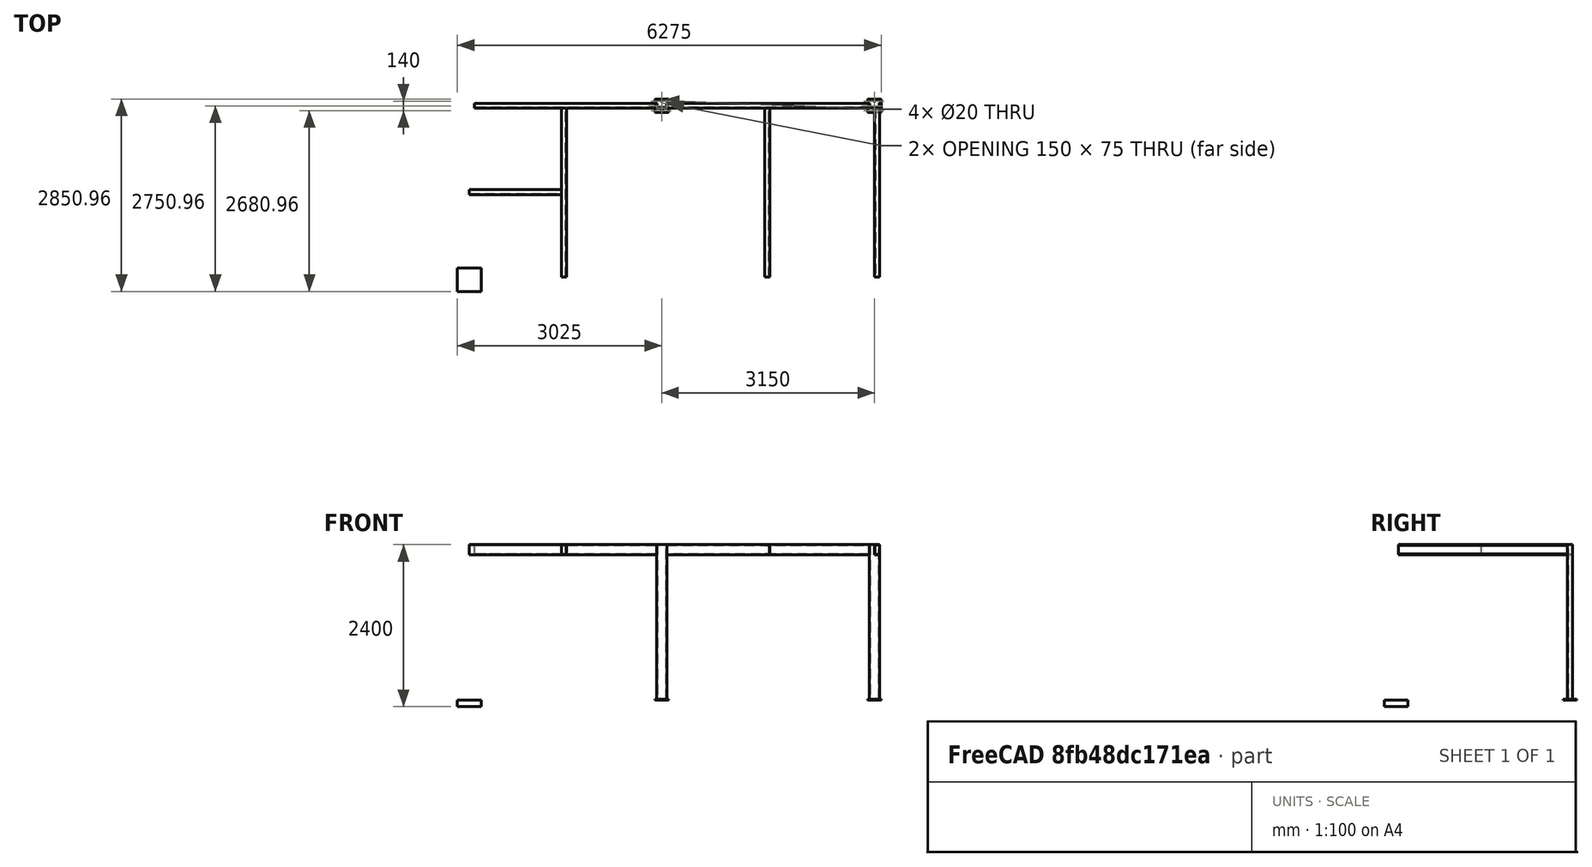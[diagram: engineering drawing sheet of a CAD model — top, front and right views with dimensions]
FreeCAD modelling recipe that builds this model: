
FCSTD DOCUMENT  (FreeCAD 0.21R30492 (Git))
Label: test
License: All rights reserved
LicenseURL: http://en.wikipedia.org/wiki/All_rights_reserved
objects: App::FeaturePython×44, Part::FeaturePython×14, Part::Mirroring×3, Part::Extrusion×2, App::Link×2, Part::MultiFuse×1
note: 20 computed .brp shape members not serialized (recipe doc carries the construction recipe); baked Part::Feature solids carry a one-line shape summary decoded from their .brp

FEATURE [Part::FeaturePython] Rectang  # WARN: FeaturePython — macro-defined, semantics opaque (R4)
  B = 350
  H = 350
  sface = 0
FEATURE [Part::Extrusion] Extrude
  Base = -> Rectang
  Dir = (0,0,-1)
  DirMode = 2
  FaceMakerClass = Part::FaceMakerBullseye
  LengthFwd = 100
  LengthRev = 0
  Solid = false
  Symmetric = false
FEATURE [Part::FeaturePython] Extrude_001  # a2plus imported part (geometry in sourceFile) (typed FeaturePython)
  a2p_Version = 0.4.60i
  fixedPosition = true
  localSourceObject = Extrude
  objectType = a2pPart
  sourceFile = converted
  subassemblyImport = false
  timeLastImport = 1.67808e+09
  updateColors = true
FEATURE [Part::FeaturePython] BasePlate  # WARN: FeaturePython — macro-defined, semantics opaque (R4)
  B = 200
  D = 20
  H = 200
  b1 = 30
  h1 = 100
  sface = 0
FEATURE [Part::FeaturePython] C150x75x6  label="SS"  # WARN: FeaturePython — macro-defined, semantics opaque (R4)
  L = 2300
  Solid = true
  size = 3
  standard = SS
  expr: Label = standard
FEATURE [Part::Extrusion] Extrude001
  Base = -> BasePlate
  Dir = (0,0,1)
  DirMode = 2
  FaceMakerClass = Part::FaceMakerBullseye
  LengthFwd = 9
  LengthRev = 0
  Solid = true
  Symmetric = false
FEATURE [Part::MultiFuse] Fusion  label="C-shaped steel"
  Placement = pos=(-7.12519e-09,0.956326,3.2e-14) rot=(0,0,-1;1.5708rad)
  Shapes = -> [C150x75x6,Extrude001]
FEATURE [App::FeaturePython] centerOfMass_001  label="centerOfMass_001__Extrude_001"  # a2plus constraint (typed FeaturePython)
  Object1 = Fusion
  Object2 = Extrude_001
  ParentTreeObject = -> Fusion
  SubElement1 = Face2
  SubElement2 = Face5
  Suppressed = false
  Type = CenterOfMass
  directionConstraint = 1
  lockRotation = false
  offset = 0
FEATURE [App::FeaturePython] centerOfMass_001_mirror  label="centerOfMass_001__C-shaped steel"  # a2plus constraint (typed FeaturePython)
  Object1 = Fusion
  Object2 = Extrude_001
  ParentTreeObject = -> Extrude_001
  SubElement1 = Face2
  SubElement2 = Face5
  Suppressed = false
  Type = CenterOfMass
  directionConstraint = 1
  lockRotation = false
  offset = 0
FEATURE [Part::FeaturePython] C150x75x007  label="Channel"  # WARN: FeaturePython — macro-defined, semantics opaque (R4)
  L = 2700
  Placement = pos=(2775,0.956326,2225) rot=(0.57735,-0.57735,-0.57735;2.0944rad)
  Solid = true
  size = 3
  standard = SS
FEATURE [App::FeaturePython] pointIdentity_001  label="pointIdentity_001__C-shaped steel"  # a2plus constraint (typed FeaturePython)
  Object1 = C150x75x007
  Object2 = Fusion
  ParentTreeObject = -> C150x75x007
  SubElement1 = Vertex2
  SubElement2 = Vertex38
  Suppressed = false
  Type = pointIdentity
FEATURE [App::FeaturePython] pointIdentity_001_mirror  label="pointIdentity_001__Channel"  # a2plus constraint (typed FeaturePython)
  Object1 = C150x75x007
  Object2 = Fusion
  ParentTreeObject = -> Fusion
  SubElement1 = Vertex2
  SubElement2 = Vertex38
  Suppressed = false
  Type = pointIdentity
FEATURE [App::Link] Link  label="C-shaped steel001"
  LinkPlacement = pos=(2850,0.956314,-1.98657e-07) rot=(0,0,-1;1.5708rad)
  LinkedObject = -> Fusion
  Placement = pos=(2850,0.956314,-1.98657e-07) rot=(0,0,-1;1.5708rad)
FEATURE [App::FeaturePython] pointIdentity_002  label="pointIdentity_002__C-shaped steel001"  # a2plus constraint (typed FeaturePython)
  Object1 = C150x75x007
  Object2 = Link
  ParentTreeObject = -> C150x75x007
  SubElement1 = Vertex1
  SubElement2 = Vertex37
  Suppressed = false
  Type = pointIdentity
FEATURE [App::FeaturePython] pointIdentity_002_mirror  label="pointIdentity_002__Channel"  # a2plus constraint (typed FeaturePython)
  Object1 = C150x75x007
  Object2 = Link
  ParentTreeObject = -> Link
  SubElement1 = Vertex1
  SubElement2 = Vertex37
  Suppressed = false
  Type = pointIdentity
FEATURE [Part::FeaturePython] C150x75x008  label="Channel001"  # WARN: FeaturePython — macro-defined, semantics opaque (R4)
  L = 3000
  Placement = pos=(5925,0.956301,2225) rot=(0.57735,-0.57735,-0.57735;2.0944rad)
  Solid = true
  size = 3
  standard = SS
FEATURE [App::FeaturePython] pointIdentity_003  label="pointIdentity_003__C-shaped steel001"  # a2plus constraint (typed FeaturePython)
  Object1 = C150x75x008
  Object2 = Link
  ParentTreeObject = -> C150x75x008
  SubElement1 = Vertex2
  SubElement2 = Vertex38
  Suppressed = false
  Type = pointIdentity
FEATURE [App::FeaturePython] pointIdentity_003_mirror  label="pointIdentity_003__Channel001"  # a2plus constraint (typed FeaturePython)
  Object1 = C150x75x008
  Object2 = Link
  ParentTreeObject = -> Link
  SubElement1 = Vertex2
  SubElement2 = Vertex38
  Suppressed = false
  Type = pointIdentity
FEATURE [App::Link] Link001  label="C-shaped steel002"
  LinkPlacement = pos=(6000,0.956288,-2.23239e-07) rot=(0,0,-1;1.5708rad)
  LinkedObject = -> Link
  Placement = pos=(6000,0.956288,-2.23239e-07) rot=(0,0,-1;1.5708rad)
FEATURE [App::FeaturePython] pointIdentity_004  label="pointIdentity_004__Channel001"  # a2plus constraint (typed FeaturePython)
  Object1 = Link001
  Object2 = C150x75x008
  ParentTreeObject = -> Link001
  SubElement1 = Vertex37
  SubElement2 = Vertex1
  Suppressed = false
  Type = pointIdentity
FEATURE [App::FeaturePython] pointIdentity_004_mirror  label="pointIdentity_004__C-shaped steel002"  # a2plus constraint (typed FeaturePython)
  Object1 = Link001
  Object2 = C150x75x008
  ParentTreeObject = -> C150x75x008
  SubElement1 = Vertex37
  SubElement2 = Vertex1
  Suppressed = false
  Type = pointIdentity
FEATURE [Part::FeaturePython] C150x75x009  label="Channel002"  # WARN: FeaturePython — macro-defined, semantics opaque (R4)
  L = 2500
  Placement = pos=(-37.5,38.4563,2225) rot=(0,0.707107,0.707107;3.14159rad)
  Solid = true
  size = 3
  standard = SS
FEATURE [App::FeaturePython] pointIdentity_005  label="pointIdentity_005__C-shaped steel"  # a2plus constraint (typed FeaturePython)
  Object1 = C150x75x009
  Object2 = Fusion
  ParentTreeObject = -> C150x75x009
  SubElement1 = Vertex23
  SubElement2 = Vertex37
  Suppressed = false
  Type = pointIdentity
FEATURE [App::FeaturePython] pointIdentity_005_mirror  label="pointIdentity_005__Channel002"  # a2plus constraint (typed FeaturePython)
  Object1 = C150x75x009
  Object2 = Fusion
  ParentTreeObject = -> Fusion
  SubElement1 = Vertex23
  SubElement2 = Vertex37
  Suppressed = false
  Type = pointIdentity
FEATURE [Part::FeaturePython] Clone  label="Channel003"  # Draft clone (typed FeaturePython)
  AttacherType = Attacher::AttachEngine3D
  Fuse = false
  Objects = -> [C150x75x009]
  Placement = pos=(2850,38.4563,2225) rot=(0,0.707107,0.707107;3.14159rad)
  Scale = (1,1,1)
FEATURE [App::FeaturePython] pointOnLine_001  label="pointOnLine_001__C-shaped steel001"  # a2plus constraint (typed FeaturePython)
  Object1 = Clone
  Object2 = Link
  ParentTreeObject = -> Clone
  SubElement1 = Vertex1
  SubElement2 = Edge44
  Suppressed = false
  Type = pointOnLine
FEATURE [App::FeaturePython] pointOnLine_001_mirror  label="pointOnLine_001__Channel003"  # a2plus constraint (typed FeaturePython)
  Object1 = Clone
  Object2 = Link
  ParentTreeObject = -> Link
  SubElement1 = Vertex1
  SubElement2 = Edge44
  Suppressed = false
  Type = pointOnLine
FEATURE [App::FeaturePython] planeCoincident_001  label="planeCoincident_001__C-shaped steel001"  # a2plus constraint (typed FeaturePython)
  Object1 = Clone
  Object2 = Link
  ParentTreeObject = -> Clone
  SubElement1 = Face1
  SubElement2 = Face21
  Suppressed = false
  Type = plane
  directionConstraint = 0
  offset = 37.5
FEATURE [App::FeaturePython] planeCoincident_001_mirror  label="planeCoincident_001__Channel003"  # a2plus constraint (typed FeaturePython)
  Object1 = Clone
  Object2 = Link
  ParentTreeObject = -> Link
  SubElement1 = Face1
  SubElement2 = Face21
  Suppressed = false
  Type = plane
  directionConstraint = 0
  offset = 37.5
FEATURE [Part::FeaturePython] Clone001  label="Channel004"  # Draft clone (typed FeaturePython)
  AttacherType = Attacher::AttachEngine3D
  Fuse = false
  Objects = -> [Clone]
  Placement = pos=(6037.5,2538.46,2225) rot=(1,0,0;1.5708rad)
  Scale = (1,1,1)
FEATURE [App::FeaturePython] pointIdentity_006  label="pointIdentity_006__Channel004"  # a2plus constraint (typed FeaturePython)
  Object1 = Link001
  Object2 = Clone001
  ParentTreeObject = -> Link001
  SubElement1 = Vertex38
  SubElement2 = Vertex24
  Suppressed = false
  Type = pointIdentity
FEATURE [App::FeaturePython] pointIdentity_006_mirror  label="pointIdentity_006__C-shaped steel002"  # a2plus constraint (typed FeaturePython)
  Object1 = Link001
  Object2 = Clone001
  ParentTreeObject = -> Clone001
  SubElement1 = Vertex38
  SubElement2 = Vertex24
  Suppressed = false
  Type = pointIdentity
FEATURE [Part::FeaturePython] Clone002  label="C-shaped steel003"  # Draft clone (typed FeaturePython)
  AttacherType = Attacher::AttachEngine3D
  Fuse = false
  Objects = -> [Fusion]
  Placement = pos=(0.00420855,2575.96,5.04641e-05) rot=(-1e-06,-1e-06,1;1.5708rad)
  Scale = (1,1,1)
FEATURE [App::FeaturePython] pointIdentity_007  label="pointIdentity_007__Channel002"  # a2plus constraint (typed FeaturePython)
  Object1 = Clone002
  Object2 = C150x75x009
  ParentTreeObject = -> Clone002
  SubElement1 = Vertex38
  SubElement2 = Vertex24
  Suppressed = false
  Type = pointIdentity
FEATURE [App::FeaturePython] pointIdentity_007_mirror  label="pointIdentity_007__C-shaped steel003"  # a2plus constraint (typed FeaturePython)
  Object1 = Clone002
  Object2 = C150x75x009
  ParentTreeObject = -> C150x75x009
  SubElement1 = Vertex38
  SubElement2 = Vertex24
  Suppressed = false
  Type = pointIdentity
FEATURE [Part::FeaturePython] Clone003  label="C-shaped steel004"  # Draft clone (typed FeaturePython)
  AttacherType = Attacher::AttachEngine3D
  Fuse = false
  Objects = -> [Clone002]
  Placement = pos=(2850,2575.96,0.000160857) rot=(0,0,1;1.5708rad)
  Scale = (1,1,1)
FEATURE [App::FeaturePython] planeCoincident_002  label="planeCoincident_002__Channel003"  # a2plus constraint (typed FeaturePython)
  Object1 = Clone003
  Object2 = Clone
  ParentTreeObject = -> Clone003
  SubElement1 = Face11
  SubElement2 = Face1
  Suppressed = false
  Type = plane
  directionConstraint = 0
  offset = -37.5
FEATURE [App::FeaturePython] planeCoincident_002_mirror  label="planeCoincident_002__C-shaped steel004"  # a2plus constraint (typed FeaturePython)
  Object1 = Clone003
  Object2 = Clone
  ParentTreeObject = -> Clone
  SubElement1 = Face11
  SubElement2 = Face1
  Suppressed = false
  Type = plane
  directionConstraint = 0
  offset = -37.5
FEATURE [Part::Mirroring] mirror  label="Channel (mirrored) "
  Base = (-7.12504e-09,1288.46,2300)
  Normal = (-2.6766e-09,-1,0)
  Placement = pos=(-6.69189e-06,4.01514e-07,0.000100336) rot=(0,0,1;0rad)
  Source = -> C150x75x007
FEATURE [App::FeaturePython] pointIdentity_008  label="pointIdentity_008__C-shaped steel003"  # a2plus constraint (typed FeaturePython)
  Object1 = mirror
  Object2 = Clone002
  ParentTreeObject = -> mirror
  SubElement1 = Vertex2
  SubElement2 = Vertex37
  Suppressed = false
  Type = pointIdentity
FEATURE [App::FeaturePython] pointIdentity_008_mirror  label="pointIdentity_008__Channel (mirrored) "  # a2plus constraint (typed FeaturePython)
  Object1 = mirror
  Object2 = Clone002
  ParentTreeObject = -> Clone002
  SubElement1 = Vertex2
  SubElement2 = Vertex37
  Suppressed = false
  Type = pointIdentity
FEATURE [Part::Mirroring] mirror001  label="Channel001 (mirrored) "
  Base = (2870.13,1288.46,2189.53)
  Normal = (-9.07043e-09,-1,0)
  Placement = pos=(0.000400686,2.25227e-05,0.000250762) rot=(0,0,1;0rad)
  Source = -> C150x75x008
FEATURE [App::FeaturePython] pointIdentity_009  label="pointIdentity_009__C-shaped steel004"  # a2plus constraint (typed FeaturePython)
  Object1 = mirror001
  Object2 = Clone003
  ParentTreeObject = -> mirror001
  SubElement1 = Vertex2
  SubElement2 = Vertex37
  Suppressed = false
  Type = pointIdentity
FEATURE [App::FeaturePython] pointIdentity_009_mirror  label="pointIdentity_009__Channel001 (mirrored) "  # a2plus constraint (typed FeaturePython)
  Object1 = mirror001
  Object2 = Clone003
  ParentTreeObject = -> Clone003
  SubElement1 = Vertex2
  SubElement2 = Vertex37
  Suppressed = false
  Type = pointIdentity
FEATURE [Part::Mirroring] mirror002  label="C-shaped steel002 (mirrored) "
  Base = (2870.13,1288.46,2189.53)
  Normal = (-6.98352e-09,-1,0)
  Placement = pos=(0.000363814,-2.37563e-05,3.179e-06) rot=(0,0,1;0rad)
  Source = -> Link001
FEATURE [App::FeaturePython] pointIdentity_010  label="pointIdentity_010__Channel004"  # a2plus constraint (typed FeaturePython)
  Object1 = mirror002
  Object2 = Clone001
  ParentTreeObject = -> mirror002
  SubElement1 = Vertex38
  SubElement2 = Vertex23
  Suppressed = false
  Type = pointIdentity
FEATURE [App::FeaturePython] pointIdentity_010_mirror  label="pointIdentity_010__C-shaped steel002 (mirrored) "  # a2plus constraint (typed FeaturePython)
  Object1 = mirror002
  Object2 = Clone001
  ParentTreeObject = -> Clone001
  SubElement1 = Vertex38
  SubElement2 = Vertex23
  Suppressed = false
  Type = pointIdentity
FEATURE [Part::FeaturePython] Clone004  label="Channel005"  # Draft clone (typed FeaturePython)
  AttacherType = Attacher::AttachEngine3D
  Fuse = false
  Objects = -> [C150x75x009]
  Placement = pos=(1405,38.4563,2225) rot=(0,0.707107,0.707107;3.14159rad)
  Scale = (1,1,1)
FEATURE [App::FeaturePython] planeCoincident_003  label="planeCoincident_003__Channel005"  # a2plus constraint (typed FeaturePython)
  Object1 = Clone
  Object2 = Clone004
  ParentTreeObject = -> Clone
  SubElement1 = Face1
  SubElement2 = Face1
  Suppressed = false
  Type = plane
  directionConstraint = 0
  offset = -1445
FEATURE [App::FeaturePython] planeCoincident_003_mirror  label="planeCoincident_003__Channel003"  # a2plus constraint (typed FeaturePython)
  Object1 = Clone
  Object2 = Clone004
  ParentTreeObject = -> Clone004
  SubElement1 = Face1
  SubElement2 = Face1
  Suppressed = false
  Type = plane
  directionConstraint = 0
  offset = -1445
FEATURE [Part::FeaturePython] Clone005  label="Channel006"  # Draft clone (typed FeaturePython)
  AttacherType = Attacher::AttachEngine3D
  Fuse = false
  Objects = -> [Clone]
  Placement = pos=(4415,38.4561,2225) rot=(0,0.707107,0.707107;3.14159rad)
  Scale = (1,1,1)
FEATURE [App::FeaturePython] planeCoincident_004  label="planeCoincident_004__Channel003"  # a2plus constraint (typed FeaturePython)
  Object1 = Clone005
  Object2 = Clone
  ParentTreeObject = -> Clone005
  SubElement1 = Face1
  SubElement2 = Face1
  Suppressed = false
  Type = plane
  directionConstraint = 0
  offset = -1565
FEATURE [App::FeaturePython] planeCoincident_004_mirror  label="planeCoincident_004__Channel006"  # a2plus constraint (typed FeaturePython)
  Object1 = Clone005
  Object2 = Clone
  ParentTreeObject = -> Clone
  SubElement1 = Face1
  SubElement2 = Face1
  Suppressed = false
  Type = plane
  directionConstraint = 0
  offset = -1565
FEATURE [App::FeaturePython] planeCoincident_005  label="planeCoincident_005__Channel (mirrored) "  # a2plus constraint (typed FeaturePython)
  Object1 = Clone004
  Object2 = mirror
  ParentTreeObject = -> Clone004
  SubElement1 = Face12
  SubElement2 = Face12
  Suppressed = false
  Type = plane
  directionConstraint = 0
  offset = 0
FEATURE [App::FeaturePython] planeCoincident_005_mirror  label="planeCoincident_005__Channel005"  # a2plus constraint (typed FeaturePython)
  Object1 = Clone004
  Object2 = mirror
  ParentTreeObject = -> mirror
  SubElement1 = Face12
  SubElement2 = Face12
  Suppressed = false
  Type = plane
  directionConstraint = 0
  offset = 0
FEATURE [App::FeaturePython] planeCoincident_006  label="planeCoincident_006__Channel001 (mirrored) "  # a2plus constraint (typed FeaturePython)
  Object1 = Clone005
  Object2 = mirror001
  ParentTreeObject = -> Clone005
  SubElement1 = Face12
  SubElement2 = Face12
  Suppressed = false
  Type = plane
  directionConstraint = 0
  offset = 0
FEATURE [App::FeaturePython] planeCoincident_006_mirror  label="planeCoincident_006__Channel006"  # a2plus constraint (typed FeaturePython)
  Object1 = Clone005
  Object2 = mirror001
  ParentTreeObject = -> mirror001
  SubElement1 = Face12
  SubElement2 = Face12
  Suppressed = false
  Type = plane
  directionConstraint = 0
  offset = 0
FEATURE [App::FeaturePython] planeCoincident_007  label="planeCoincident_007__C-shaped steel004"  # a2plus constraint (typed FeaturePython)
  Object1 = mirror
  Object2 = Clone003
  ParentTreeObject = -> mirror
  SubElement1 = Face12
  SubElement2 = Face22
  Suppressed = false
  Type = plane
  directionConstraint = 1
  offset = 0
FEATURE [App::FeaturePython] planeCoincident_007_mirror  label="planeCoincident_007__Channel (mirrored) "  # a2plus constraint (typed FeaturePython)
  Object1 = mirror
  Object2 = Clone003
  ParentTreeObject = -> Clone003
  SubElement1 = Face12
  SubElement2 = Face22
  Suppressed = false
  Type = plane
  directionConstraint = 1
  offset = 0
FEATURE [Part::FeaturePython] C150x75x010  label="Channel007"  # WARN: FeaturePython — macro-defined, semantics opaque (R4)
  L = 1367.5
  Placement = pos=(-7.12309e-09,1297,2225) rot=(0.57735,0.57735,0.57735;2.0944rad)
  Solid = true
  size = 3
  standard = SS
FEATURE [App::FeaturePython] planeCoincident_008  label="planeCoincident_008__Channel002"  # a2plus constraint (typed FeaturePython)
  Object1 = C150x75x010
  Object2 = C150x75x009
  ParentTreeObject = -> C150x75x010
  SubElement1 = Face12
  SubElement2 = Face12
  Suppressed = false
  Type = plane
  directionConstraint = 0
  offset = 0
FEATURE [App::FeaturePython] planeCoincident_008_mirror  label="planeCoincident_008__Channel007"  # a2plus constraint (typed FeaturePython)
  Object1 = C150x75x010
  Object2 = C150x75x009
  ParentTreeObject = -> C150x75x009
  SubElement1 = Face12
  SubElement2 = Face12
  Suppressed = false
  Type = plane
  directionConstraint = 0
  offset = 0
FEATURE [App::FeaturePython] axisCoincident_001  label="axisCoincident_001__Channel002"  # a2plus constraint (typed FeaturePython)
  Object1 = C150x75x010
  Object2 = C150x75x009
  ParentTreeObject = -> C150x75x010
  SubElement1 = Edge35
  SubElement2 = Edge1
  Suppressed = false
  Type = axial
  directionConstraint = 1
  lockRotation = false
FEATURE [App::FeaturePython] axisCoincident_001_mirror  label="axisCoincident_001__Channel007"  # a2plus constraint (typed FeaturePython)
  Object1 = C150x75x010
  Object2 = C150x75x009
  ParentTreeObject = -> C150x75x009
  SubElement1 = Edge35
  SubElement2 = Edge1
  Suppressed = false
  Type = axial
  directionConstraint = 1
  lockRotation = false
FEATURE [App::FeaturePython] planeCoincident_009  label="planeCoincident_009__Channel002"  # a2plus constraint (typed FeaturePython)
  Object1 = mirror
  Object2 = C150x75x009
  ParentTreeObject = -> mirror
  SubElement1 = Face12
  SubElement2 = Face12
  Suppressed = false
  Type = plane
  directionConstraint = 0
  offset = 0
FEATURE [App::FeaturePython] planeCoincident_009_mirror  label="planeCoincident_009__Channel (mirrored) "  # a2plus constraint (typed FeaturePython)
  Object1 = mirror
  Object2 = C150x75x009
  ParentTreeObject = -> C150x75x009
  SubElement1 = Face12
  SubElement2 = Face12
  Suppressed = false
  Type = plane
  directionConstraint = 0
  offset = 0
